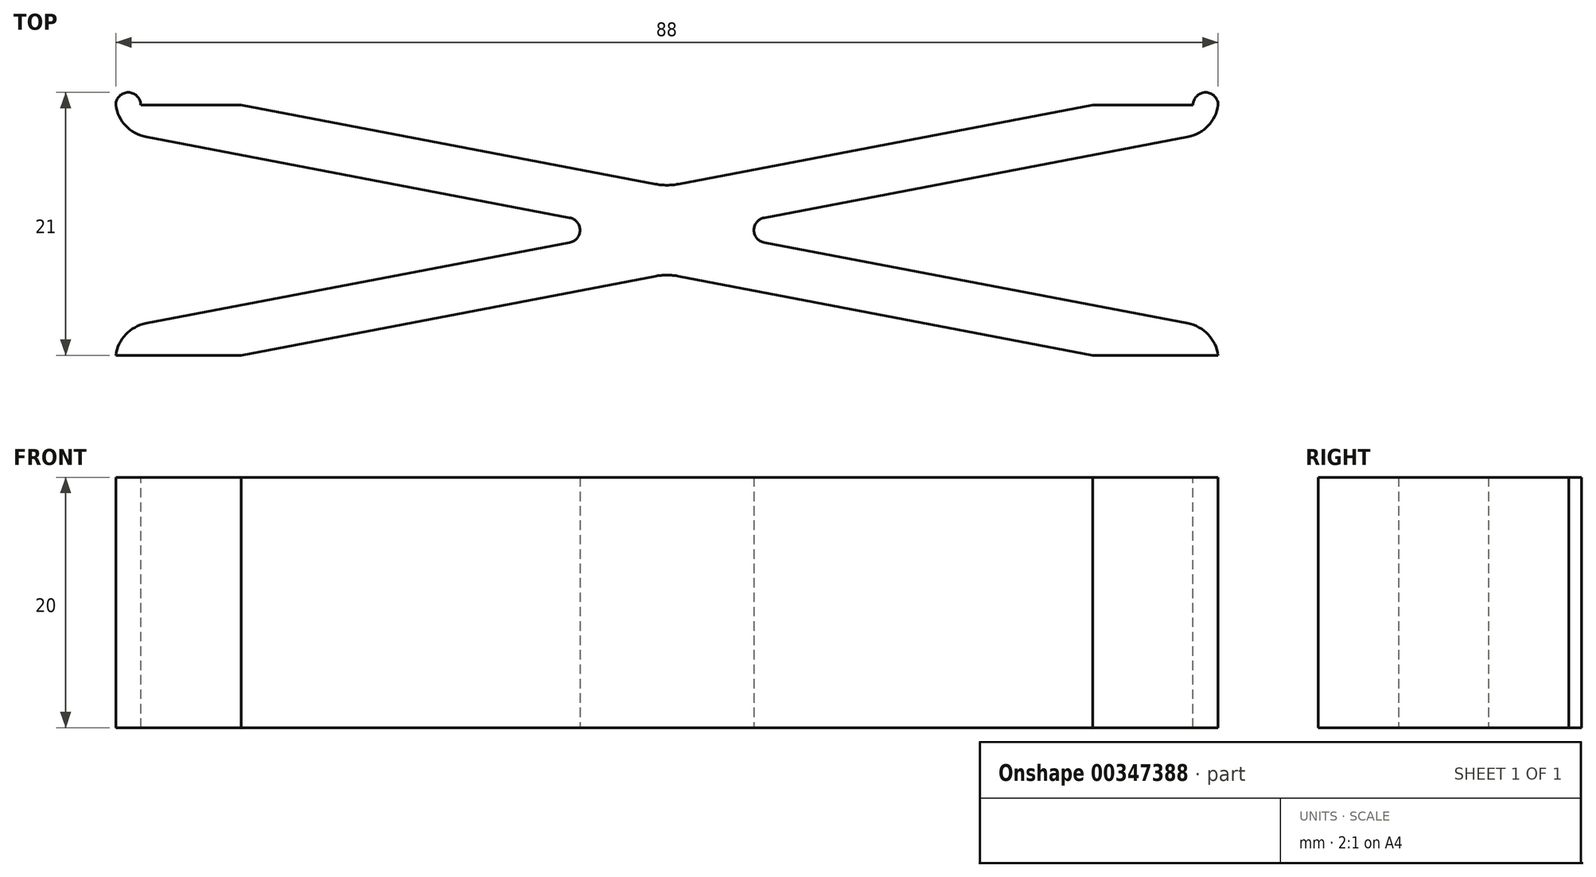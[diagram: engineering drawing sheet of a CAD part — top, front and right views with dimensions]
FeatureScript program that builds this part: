
annotation { "Feature Type Name" : "Feature", "Feature Type Description" : "" }
export const myFeature = defineFeature(function(context is Context, id is Id, definition is map)
    precondition{}
    {
        {
            var Q0;
            Q0=qCreatedBy(makeId("Top.planeOp"),FACE);
            var sketch = newSketch(context, id + "F0", { "sketchPlane" : qUnion([Q0])});
            skLineSegment(sketch, "E0", {"start": v(0, 0) * mm, "end": v(10, 0) * mm});
            skLineSegment(sketch, "E1", {"start": v(10, 0) * mm, "end": v(78, 0) * mm, "construction": true});
            skLineSegment(sketch, "E2", {"start": v(78, 0) * mm, "end": v(88, 0) * mm});
            skLineSegment(sketch, "E3", {"start": v(44, 0) * mm, "end": v(44, 6.5) * mm, "construction": true});
            skLineSegment(sketch, "E4", {"start": v(10, 0) * mm, "end": v(44, 6.5) * mm});
            skLineSegment(sketch, "E5", {"start": v(44, 6.5) * mm, "end": v(44, 13.5) * mm});
            skLineSegment(sketch, "E6", {"start": v(10, 0) * mm, "end": v(10, 20) * mm, "construction": true});
            skLineSegment(sketch, "E7", {"start": v(10, 20) * mm, "end": v(44, 13.5) * mm});
            skLineSegment(sketch, "E8", {"start": v(10, 20) * mm, "end": v(0, 20) * mm});
            skLineSegment(sketch, "E9", {"start": v(10, 20) * mm, "end": v(10, 16) * mm, "construction": true});
            skLineSegment(sketch, "E10", {"start": v(10, 0) * mm, "end": v(10, 4) * mm, "construction": true});
            skLineSegment(sketch, "E11", {"start": v(10, 4) * mm, "end": v(41.38, 10) * mm});
            skLineSegment(sketch, "E12", {"start": v(10, 16) * mm, "end": v(41.38, 10) * mm});
            skLineSegment(sketch, "E13", {"start": v(10, 16) * mm, "end": v(0, 17.91) * mm});
            skLineSegment(sketch, "E14", {"start": v(0, 17.91) * mm, "end": v(0, 20) * mm});
            skLineSegment(sketch, "E15", {"start": v(10, 4) * mm, "end": v(0, 2.09) * mm});
            skLineSegment(sketch, "E16", {"start": v(0, 2.09) * mm, "end": v(0, 0) * mm});
            skLineSegment(sketch, "E17", {"start": v(0, 20) * mm, "end": v(2, 20) * mm, "construction": true});
            skArc(sketch, "E18", {"start": v(2, 20) * mm, "mid": v(1, 21) * mm, "end": v(0, 20) * mm});
            skLineSegment(sketch, "E19", {"start": v(10, 10) * mm, "end": v(41.38, 10) * mm, "construction": true});
            skLineSegment(sketch, "E20", {"start": v(41.38, 10) * mm, "end": v(44, 10) * mm, "construction": true});
            skSolve(sketch);
        }
        {
            var Q0;
            Q0 = qSketchRegion(id + "F0", true);
            extrude(context, id + "F1", {"entities" : qUnion([Q0]), "oppositeDirection" : true, "depth" : 20 * mm});
        }
        {
            var Q0;
            Q0=makeQuery(id+"F1.opExtrude","SWEPT_EDGE",EDGE,{"disambiguationData":[OSD([sQuery(id+"F0.wireOp",EDGE,"E11"),sQuery(id+"F0.wireOp",EDGE,"E12")])]});
            fillet(context, id + "F2", {"entities" : qUnion([Q0]), "radius" : 1 * mm, "tangentPropagation" : true, "allowEdgeOverflow" : false});
        }
        {
            var Q0;
            Q0=makeQuery(id+"F1.opExtrude","SWEPT_EDGE",EDGE,{"disambiguationData":[OSD([sQuery(id+"F0.wireOp",EDGE,"E13"),sQuery(id+"F0.wireOp",EDGE,"E14")])]});
            var Q1;
            Q1=makeQuery(id+"F1.opExtrude","SWEPT_EDGE",EDGE,{"disambiguationData":[OSD([sQuery(id+"F0.wireOp",EDGE,"E15"),sQuery(id+"F0.wireOp",EDGE,"E16")])]});
            fillet(context, id + "F3", {"entities" : qUnion([Q0, Q1]), "radius" : 3 * mm, "tangentPropagation" : true, "allowEdgeOverflow" : false});
        }
        {
            var Q0;
            Q0=makeQuery(id+"F1.opExtrude","SWEPT_BODY",BODY,{"disambiguationData":[OSD([sQuery(id+"F0.wireOp",EDGE,"E0"),sQuery(id+"F0.wireOp",EDGE,"E4"),sQuery(id+"F0.wireOp",EDGE,"E5"),sQuery(id+"F0.wireOp",EDGE,"E7"),sQuery(id+"F0.wireOp",EDGE,"E8"),sQuery(id+"F0.wireOp",EDGE,"E11"),sQuery(id+"F0.wireOp",EDGE,"E12"),sQuery(id+"F0.wireOp",EDGE,"E13"),sQuery(id+"F0.wireOp",EDGE,"E15"),sQuery(id+"F0.wireOp",EDGE,"E16"),sQuery(id+"F0.wireOp",EDGE,"kvz6pTU9-0PWJ-05ta-KlW9-T2WsR2k4i022"),sQuery(id+"F0.wireOp",EDGE,"50u14uMf-E9CO-359f-qUIs-hp0JfSUj06k2"),sQuery(id+"F0.wireOp",EDGE,"KEhGEAyb-vElv-mRMH-MCMv-bNV8kqBgBv1z")])]});
            var Q1;
            Q1=makeQuery(id+"F1.opExtrude","SWEPT_FACE",FACE,{"disambiguationData":[OSD([sQuery(id+"F0.wireOp",EDGE,"E5")])]});
            mirror(context, id + "F4", {"operationType" : NewBodyOperationType.ADD, "entities" : qUnion([Q0]), "mirrorPlane" : qUnion([Q1])});
        }
        {
            var Q0;
            {var subQ0=makeQuery(id+"F1.opExtrude","SWEPT_EDGE",EDGE,{"disambiguationData":[OSD([sQuery(id+"F0.wireOp",EDGE,"E5"),sQuery(id+"F0.wireOp",EDGE,"E7")])]});Q0=makeQuery(id+"F4.boolean.opBoolean","MERGE",EDGE,{"derivedFrom":[subQ0,makeQuery(id+"F4.opPattern","COPY",EDGE,{"derivedFrom":subQ0,"instanceName":"1"})]});}
            var Q1;
            {var subQ0=makeQuery(id+"F1.opExtrude","SWEPT_EDGE",EDGE,{"disambiguationData":[OSD([sQuery(id+"F0.wireOp",EDGE,"E4"),sQuery(id+"F0.wireOp",EDGE,"E5")])]});Q1=makeQuery(id+"F4.boolean.opBoolean","MERGE",EDGE,{"derivedFrom":[subQ0,makeQuery(id+"F4.opPattern","COPY",EDGE,{"derivedFrom":subQ0,"instanceName":"1"})]});}
            fillet(context, id + "F5", {"entities" : qUnion([Q0, Q1]), "radius" : 5 * mm, "tangentPropagation" : true, "allowEdgeOverflow" : false});
        }
    });
